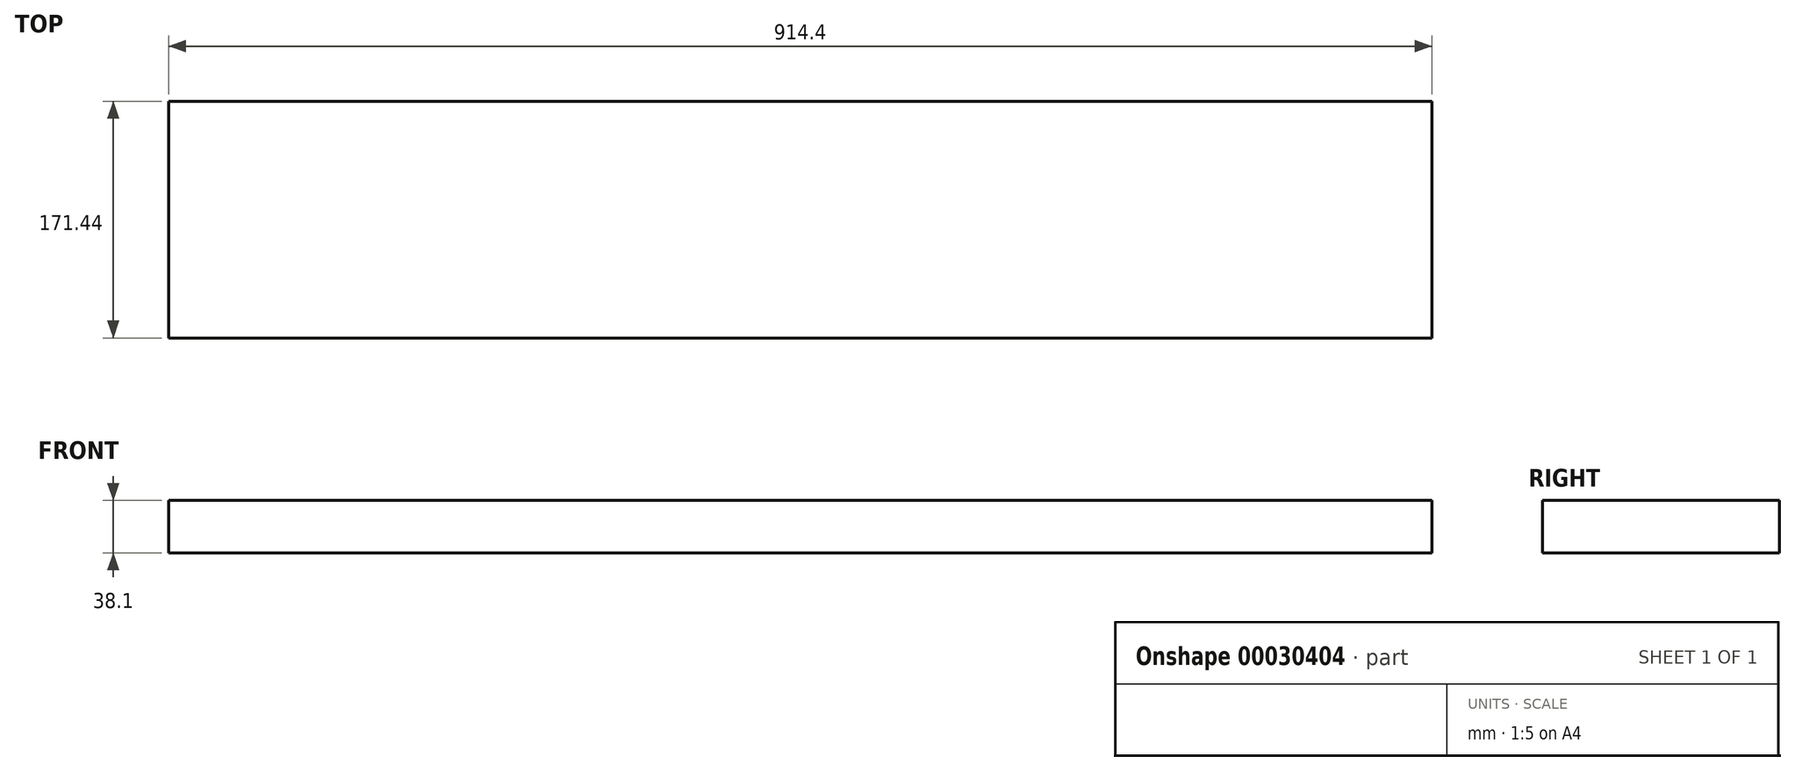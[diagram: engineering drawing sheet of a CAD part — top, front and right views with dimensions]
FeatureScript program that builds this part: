
annotation { "Feature Type Name" : "Feature", "Feature Type Description" : "" }
export const myFeature = defineFeature(function(context is Context, id is Id, definition is map)
    precondition{}
    {
        {
            var Q0;
            Q0=qCreatedBy(makeId("Top.planeOp"),FACE);
            var sketch = newSketch(context, id + "F0", { "sketchPlane" : qUnion([Q0])});
            skLineSegment(sketch, "E0.rect.bottom", {"start": v(457.2, 85.73) * mm, "end": v(-457.2, 85.73) * mm});
            skLineSegment(sketch, "E0.rect.top", {"start": v(457.2, -85.73) * mm, "end": v(-457.2, -85.73) * mm});
            skLineSegment(sketch, "E0.rect.left", {"start": v(457.2, 85.73) * mm, "end": v(457.2, -85.73) * mm});
            skLineSegment(sketch, "E0.rect.right", {"start": v(-457.2, 85.73) * mm, "end": v(-457.2, -85.73) * mm});
            skPoint(sketch, "E0.rect.middle", {"position": v(0, 0) * mm});
            skSolve(sketch);
        }
        {
            var Q0;
            Q0=makeQuery(id+"F0.imprint","IMPRINT",FACE,{"disambiguationData":[TD([[makeQuery(id+"F0.imprint","IMPRINT",EDGE,{"derivedFrom":sQuery(id+"F0.wireOp",EDGE,"E0.rect.bottom")}),1.0]])]});
            extrude(context, id + "F1", {"entities" : qUnion([Q0]), "endBound" : BoundingType.SYMMETRIC, "depth" : 38.1 * mm});
        }
    });
